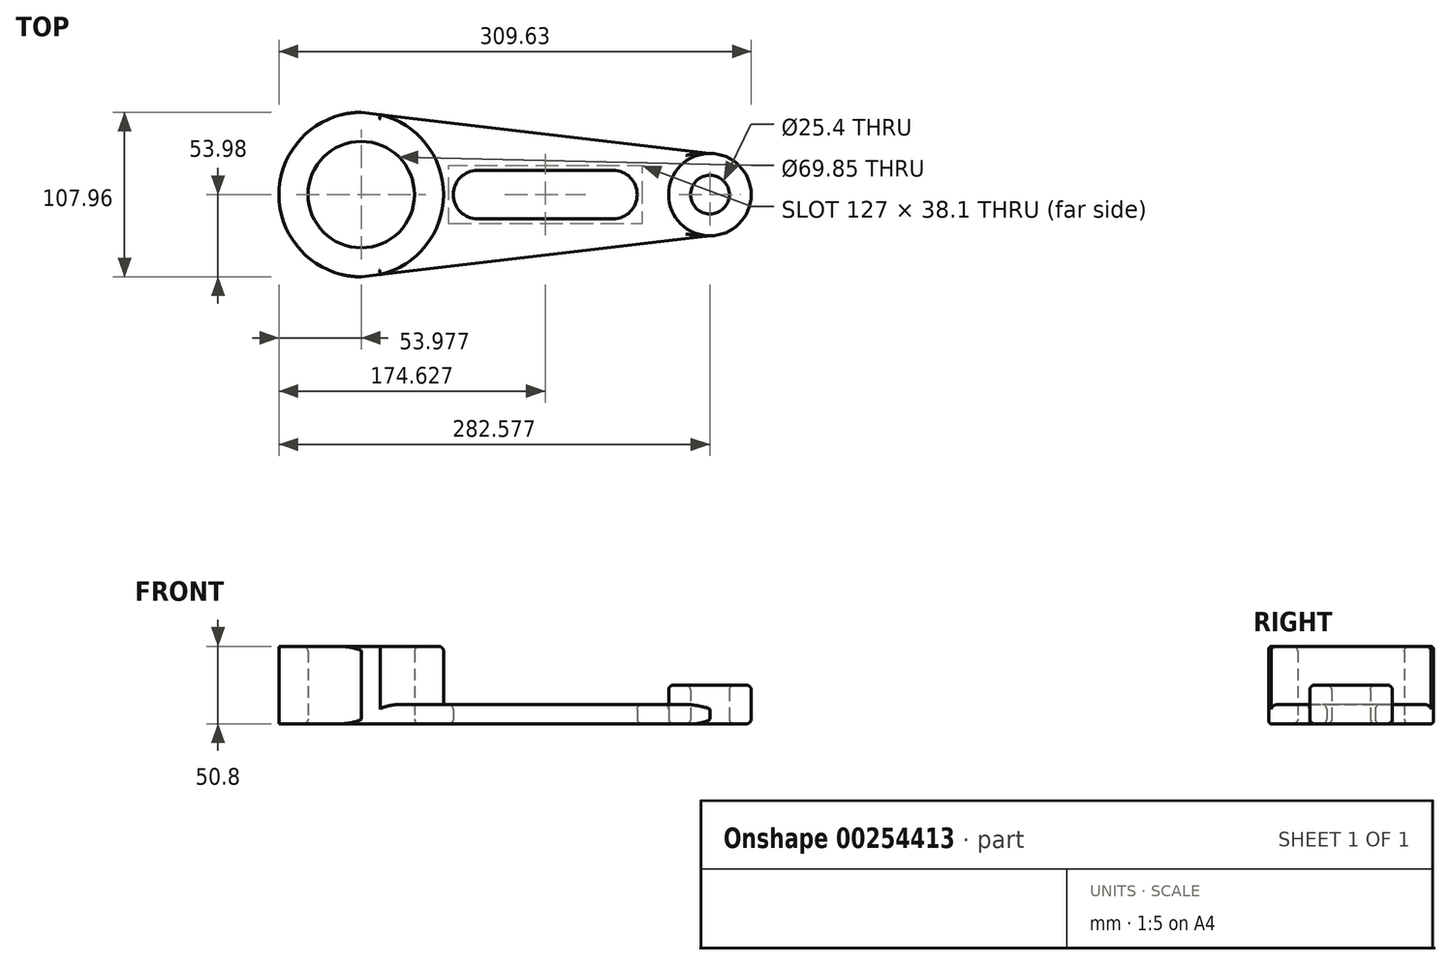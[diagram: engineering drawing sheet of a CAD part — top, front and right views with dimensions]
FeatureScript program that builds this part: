
annotation { "Feature Type Name" : "Feature", "Feature Type Description" : "" }
export const myFeature = defineFeature(function(context is Context, id is Id, definition is map)
    precondition{}
    {
        {
            var Q0;
            Q0=qCreatedBy(makeId("Top.planeOp"),FACE);
            var sketch = newSketch(context, id + "F0", { "sketchPlane" : qUnion([Q0])});
            skCircle(sketch, "E0", {"center": v(-118.92, 0) * mm, "radius": 34.93 * mm});
            skCircle(sketch, "E1", {"center": v(109.68, 0) * mm, "radius": 12.7 * mm});
            skCircle(sketch, "E2", {"center": v(-118.92, 0) * mm, "radius": 53.98 * mm});
            skCircle(sketch, "E3", {"center": v(109.68, 0) * mm, "radius": 27.05 * mm});
            skLineSegment(sketch, "E4", {"start": v(-118.92, -53.97) * mm, "end": v(109.68, -27.05) * mm});
            skCircle(sketch, "E5", {"center": v(-42.72, 0) * mm, "radius": 15.88 * mm});
            skCircle(sketch, "E6", {"center": v(46.18, 0) * mm, "radius": 15.88 * mm});
            skLineSegment(sketch, "E7", {"start": v(-42.72, 15.88) * mm, "end": v(46.18, 15.88) * mm});
            skLineSegment(sketch, "E8", {"start": v(-42.72, -15.88) * mm, "end": v(46.18, -15.88) * mm});
            skLineSegment(sketch, "E9", {"start": v(136.73, 0) * mm, "end": v(-172.9, 0) * mm});
            skLineSegment(sketch, "E10", {"start": v(-118.92, 53.97) * mm, "end": v(109.68, 27.05) * mm});
            skSolve(sketch);
        }
        {
            var Q0;
            {var subQ4=sQuery(id+"F0.wireOp",EDGE,"E9");var subQ7=sQuery(id+"F0.wireOp",EDGE,"E0");var subQ8=makeQuery(id+"F0.imprint","INTERSECT",VERTEX,{"disambiguationData":[OD(0.0)],"derivedFrom":[subQ7,subQ4]});Q0=makeQuery(id+"F0.imprint","IMPRINT",FACE,{"disambiguationData":[TD([[makeQuery(id+"F0.imprint","IMPRINT",EDGE,{"disambiguationData":[TD([[subQ8,-1.0]])],"derivedFrom":subQ7}),-1.0]])]});}
            var Q1;
            {var subQ4=sQuery(id+"F0.wireOp",EDGE,"E9");var subQ7=sQuery(id+"F0.wireOp",EDGE,"E0");var subQ8=makeQuery(id+"F0.imprint","INTERSECT",VERTEX,{"disambiguationData":[OD(0.0)],"derivedFrom":[subQ7,subQ4]});Q1=makeQuery(id+"F0.imprint","IMPRINT",FACE,{"disambiguationData":[TD([[makeQuery(id+"F0.imprint","IMPRINT",EDGE,{"disambiguationData":[TD([[subQ8,1.0]])],"derivedFrom":subQ7}),-1.0]])]});}
            extrude(context, id + "F1", {"entities" : qUnion([Q0, Q1]), "depth" : 50.8 * mm});
        }
        {
            var Q0;
            {var subQ0=sQuery(id+"F0.wireOp",EDGE,"E9");var subQ1=sQuery(id+"F0.wireOp",EDGE,"E1");var subQ2=makeQuery(id+"F0.imprint","INTERSECT",VERTEX,{"disambiguationData":[OD(0.0)],"derivedFrom":[subQ1,subQ0]});Q0=makeQuery(id+"F0.imprint","IMPRINT",FACE,{"disambiguationData":[TD([[makeQuery(id+"F0.imprint","IMPRINT",EDGE,{"disambiguationData":[TD([[subQ2,-1.0]])],"derivedFrom":subQ1}),-1.0]])]});}
            var Q1;
            {var subQ2=sQuery(id+"F0.wireOp",EDGE,"E9");var subQ4=sQuery(id+"F0.wireOp",EDGE,"E1");var subQ5=makeQuery(id+"F0.imprint","INTERSECT",VERTEX,{"disambiguationData":[OD(0.0)],"derivedFrom":[subQ4,subQ2]});Q1=makeQuery(id+"F0.imprint","IMPRINT",FACE,{"disambiguationData":[TD([[makeQuery(id+"F0.imprint","IMPRINT",EDGE,{"disambiguationData":[TD([[subQ5,1.0]])],"derivedFrom":subQ4}),-1.0]])]});}
            extrude(context, id + "F2", {"entities" : qUnion([Q0, Q1]), "depth" : 25.4 * mm});
        }
        {
            var Q0;
            {var subQ0=sQuery(id+"F0.wireOp",EDGE,"E8");Q0=makeQuery(id+"F0.imprint","IMPRINT",FACE,{"disambiguationData":[TD([[makeQuery(id+"F0.imprint","IMPRINT",EDGE,{"derivedFrom":subQ0}),-1.0]])]});}
            var Q1;
            {var subQ0=sQuery(id+"F0.wireOp",EDGE,"E7");Q1=makeQuery(id+"F0.imprint","IMPRINT",FACE,{"disambiguationData":[TD([[makeQuery(id+"F0.imprint","IMPRINT",EDGE,{"derivedFrom":subQ0}),1.0]])]});}
            extrude(context, id + "F3", {"entities" : qUnion([Q0, Q1]), "depth" : 12.7 * mm});
        }
        {
            var Q0;
            {var subQ0=sQuery(id+"F0.wireOp",EDGE,"E4");var subQ1=sQuery(id+"F0.wireOp",EDGE,"E2");var subQ2=makeQuery(id+"F0.imprint","INTERSECT",VERTEX,{"disambiguationData":[OD(0.0)],"derivedFrom":[subQ1,subQ0]});Q0=makeQuery(id+"F0.imprint","IMPRINT",FACE,{"disambiguationData":[TD([[makeQuery(id+"F0.imprint","IMPRINT",EDGE,{"disambiguationData":[TD([[subQ2,-1.0]])],"derivedFrom":subQ1}),1.0]])]});}
            var Q1;
            {var subQ0=sQuery(id+"F0.wireOp",EDGE,"E10");var subQ1=sQuery(id+"F0.wireOp",EDGE,"E2");var subQ2=makeQuery(id+"F0.imprint","INTERSECT",VERTEX,{"disambiguationData":[OD(0.0)],"derivedFrom":[subQ1,subQ0]});Q1=makeQuery(id+"F0.imprint","IMPRINT",FACE,{"disambiguationData":[TD([[makeQuery(id+"F0.imprint","IMPRINT",EDGE,{"disambiguationData":[TD([[subQ2,1.0]])],"derivedFrom":subQ1}),1.0]])]});}
            extrude(context, id + "F4", {"entities" : qUnion([Q0, Q1]), "operationType" : NewBodyOperationType.ADD, "depth" : 25.4 * mm});
        }
        {
            var Q0;
            Q0=makeQuery(id+"F2.opExtrude","CAP_EDGE",EDGE,{"disambiguationData":[OSD([sQuery(id+"F0.wireOp",EDGE,"E1")])],"isStart":false});
            var Q1;
            Q1=makeQuery(id+"F2.opExtrude","CAP_EDGE",EDGE,{"disambiguationData":[OSD([sQuery(id+"F0.wireOp",EDGE,"E3")])],"isStart":false});
            var Q2;
            Q2=makeQuery(id+"F3.opExtrude","CAP_EDGE",EDGE,{"disambiguationData":[OSD([sQuery(id+"F0.wireOp",EDGE,"E3")])],"isStart":false});
            var Q3;
            Q3=makeQuery(id+"F3.opExtrude","CAP_EDGE",EDGE,{"disambiguationData":[OSD([sQuery(id+"F0.wireOp",EDGE,"E2")])],"isStart":false});
            var Q4;
            Q4=makeQuery(id+"F3.opExtrude","CAP_EDGE",EDGE,{"disambiguationData":[OSD([sQuery(id+"F0.wireOp",EDGE,"E4")])],"isStart":false});
            var Q5;
            Q5=makeQuery(id+"F3.opExtrude","CAP_EDGE",EDGE,{"disambiguationData":[OSD([sQuery(id+"F0.wireOp",EDGE,"E4")])],"isStart":true});
            var Q6;
            Q6=makeQuery(id+"F3.opExtrude","CAP_EDGE",EDGE,{"disambiguationData":[OSD([sQuery(id+"F0.wireOp",EDGE,"E5")])],"isStart":false});
            var Q7;
            Q7=makeQuery(id+"F3.opExtrude","CAP_EDGE",EDGE,{"disambiguationData":[OSD([sQuery(id+"F0.wireOp",EDGE,"E7")])],"isStart":false});
            var Q8;
            Q8=makeQuery(id+"F3.opExtrude","CAP_EDGE",EDGE,{"disambiguationData":[OSD([sQuery(id+"F0.wireOp",EDGE,"E8")])],"isStart":false});
            var Q9;
            Q9=makeQuery(id+"F3.opExtrude","CAP_EDGE",EDGE,{"disambiguationData":[OSD([sQuery(id+"F0.wireOp",EDGE,"E6")])],"isStart":false});
            var Q10;
            Q10=makeQuery(id+"F3.opExtrude","CAP_EDGE",EDGE,{"disambiguationData":[OSD([sQuery(id+"F0.wireOp",EDGE,"E7")])],"isStart":true});
            var Q11;
            Q11=makeQuery(id+"F3.opExtrude","CAP_EDGE",EDGE,{"disambiguationData":[OSD([sQuery(id+"F0.wireOp",EDGE,"E5")])],"isStart":true});
            var Q12;
            Q12=makeQuery(id+"F3.opExtrude","CAP_EDGE",EDGE,{"disambiguationData":[OSD([sQuery(id+"F0.wireOp",EDGE,"E8")])],"isStart":true});
            var Q13;
            Q13=makeQuery(id+"F3.opExtrude","CAP_EDGE",EDGE,{"disambiguationData":[OSD([sQuery(id+"F0.wireOp",EDGE,"E6")])],"isStart":true});
            var Q14;
            Q14=makeQuery(id+"F3.opExtrude","CAP_EDGE",EDGE,{"disambiguationData":[OSD([sQuery(id+"F0.wireOp",EDGE,"E10")])],"isStart":false});
            var Q15;
            Q15=makeQuery(id+"F3.opExtrude","CAP_EDGE",EDGE,{"disambiguationData":[OSD([sQuery(id+"F0.wireOp",EDGE,"E10")])],"isStart":true});
            var Q16;
            {var subQ0=sQuery(id+"F0.wireOp",EDGE,"E2");Q16=makeQuery(id+"F1.opExtrude","CAP_EDGE",EDGE,{"disambiguationData":[OSD([subQ0]),TDD([makeQuery(id+"F0.imprint","IMPRINT",EDGE,{"disambiguationData":[TD([[makeQuery(id+"F0.imprint","INTERSECT",VERTEX,{"disambiguationData":[OD(1.0)],"derivedFrom":[subQ0,sQuery(id+"F0.wireOp",EDGE,"E10")]}),1.0]])],"derivedFrom":subQ0}),makeQuery(id+"F0.imprint","IMPRINT",EDGE,{"disambiguationData":[TD([[makeQuery(id+"F0.imprint","INTERSECT",VERTEX,{"disambiguationData":[OD(1.0)],"derivedFrom":[subQ0,sQuery(id+"F0.wireOp",EDGE,"E4")]}),-1.0]])],"derivedFrom":subQ0})])],"isStart":false});}
            var Q17;
            Q17=makeQuery(id+"F1.opExtrude","CAP_EDGE",EDGE,{"disambiguationData":[OSD([sQuery(id+"F0.wireOp",EDGE,"E0")])],"isStart":false});
            var Q18;
            {var subQ0=sQuery(id+"F0.wireOp",EDGE,"E2");var subQ1=makeQuery(id+"F0.imprint","INTERSECT",VERTEX,{"disambiguationData":[OD(0.0)],"derivedFrom":[subQ0,sQuery(id+"F0.wireOp",EDGE,"E9")]});Q18=makeQuery(id+"F1.opExtrude","CAP_EDGE",EDGE,{"disambiguationData":[OSD([subQ0]),TDD([makeQuery(id+"F0.imprint","IMPRINT",EDGE,{"disambiguationData":[TD([[subQ1,1.0]])],"derivedFrom":subQ0}),makeQuery(id+"F0.imprint","IMPRINT",EDGE,{"disambiguationData":[TD([[makeQuery(id+"F0.imprint","INTERSECT",VERTEX,{"disambiguationData":[OD(0.0)],"derivedFrom":[subQ0,sQuery(id+"F0.wireOp",EDGE,"E4")]}),1.0]])],"derivedFrom":subQ0})])],"isStart":false});}
            var Q19;
            {var subQ0=sQuery(id+"F0.wireOp",EDGE,"E4");var subQ1=sQuery(id+"F0.wireOp",EDGE,"E2");var subQ2=makeQuery(id+"F0.imprint","INTERSECT",VERTEX,{"disambiguationData":[OD(0.0)],"derivedFrom":[subQ1,subQ0]});var subQ3=makeQuery(id+"F0.imprint","INTERSECT",VERTEX,{"disambiguationData":[OD(1.0)],"derivedFrom":[subQ1,subQ0]});var subQ4=sQuery(id+"F0.wireOp",EDGE,"E10");var subQ5=makeQuery(id+"F0.imprint","INTERSECT",VERTEX,{"disambiguationData":[OD(0.0)],"derivedFrom":[subQ1,subQ4]});var subQ6=makeQuery(id+"F0.imprint","INTERSECT",VERTEX,{"disambiguationData":[OD(1.0)],"derivedFrom":[subQ1,subQ4]});var subQ7=sQuery(id+"F0.wireOp",EDGE,"E9");var subQ8=makeQuery(id+"F0.imprint","INTERSECT",VERTEX,{"disambiguationData":[OD(0.0)],"derivedFrom":[subQ1,subQ7]});Q19=makeQuery(id+"F4.boolean.opBoolean","MERGE",EDGE,{"derivedFrom":[makeQuery(id+"F1.opExtrude","CAP_EDGE",EDGE,{"disambiguationData":[OSD([subQ1]),TDD([makeQuery(id+"F0.imprint","IMPRINT",EDGE,{"disambiguationData":[TD([[subQ6,1.0]])],"derivedFrom":subQ1}),makeQuery(id+"F0.imprint","IMPRINT",EDGE,{"disambiguationData":[TD([[subQ3,-1.0]])],"derivedFrom":subQ1})])],"isStart":true}),makeQuery(id+"F1.opExtrude","CAP_EDGE",EDGE,{"disambiguationData":[OSD([subQ1]),TDD([makeQuery(id+"F0.imprint","IMPRINT",EDGE,{"disambiguationData":[TD([[subQ8,1.0]])],"derivedFrom":subQ1}),makeQuery(id+"F0.imprint","IMPRINT",EDGE,{"disambiguationData":[TD([[subQ2,1.0]])],"derivedFrom":subQ1})])],"isStart":true}),makeQuery(id+"F4.opExtrude","CAP_EDGE",EDGE,{"disambiguationData":[OSD([subQ1]),TDD([makeQuery(id+"F0.imprint","IMPRINT",EDGE,{"disambiguationData":[TD([[subQ5,1.0]])],"derivedFrom":subQ1})])],"isStart":true}),makeQuery(id+"F4.opExtrude","CAP_EDGE",EDGE,{"disambiguationData":[OSD([subQ1]),TDD([makeQuery(id+"F0.imprint","IMPRINT",EDGE,{"disambiguationData":[TD([[subQ2,-1.0]])],"derivedFrom":subQ1})])],"isStart":true})]});}
            var Q20;
            Q20=makeQuery(id+"F1.opExtrude","CAP_EDGE",EDGE,{"disambiguationData":[OSD([sQuery(id+"F0.wireOp",EDGE,"E10")])],"isStart":false});
            var Q21;
            Q21=makeQuery(id+"F1.opExtrude","CAP_EDGE",EDGE,{"disambiguationData":[OSD([sQuery(id+"F0.wireOp",EDGE,"E4")])],"isStart":false});
            fillet(context, id + "F5", {"entities" : qUnion([Q0, Q1, Q2, Q3, Q4, Q5, Q6, Q7, Q8, Q9, Q10, Q11, Q12, Q13, Q14, Q15, Q16, Q17, Q18, Q19, Q20, Q21]), "radius" : 3.17 * mm, "tangentPropagation" : true, "allowEdgeOverflow" : false});
        }
        {
            var Q0;
            Q0=makeQuery(id+"F1.opExtrude","CAP_EDGE",EDGE,{"disambiguationData":[OSD([sQuery(id+"F0.wireOp",EDGE,"E0")])],"isStart":true});
            var Q1;
            Q1=makeQuery(id+"F2.opExtrude","CAP_EDGE",EDGE,{"disambiguationData":[OSD([sQuery(id+"F0.wireOp",EDGE,"E1")])],"isStart":true});
            var Q2;
            Q2=makeQuery(id+"F2.opExtrude","CAP_EDGE",EDGE,{"disambiguationData":[OSD([sQuery(id+"F0.wireOp",EDGE,"E3")])],"isStart":true});
            fillet(context, id + "F6", {"entities" : qUnion([Q0, Q1, Q2]), "radius" : 3.17 * mm, "tangentPropagation" : true, "allowEdgeOverflow" : false});
        }
    });
